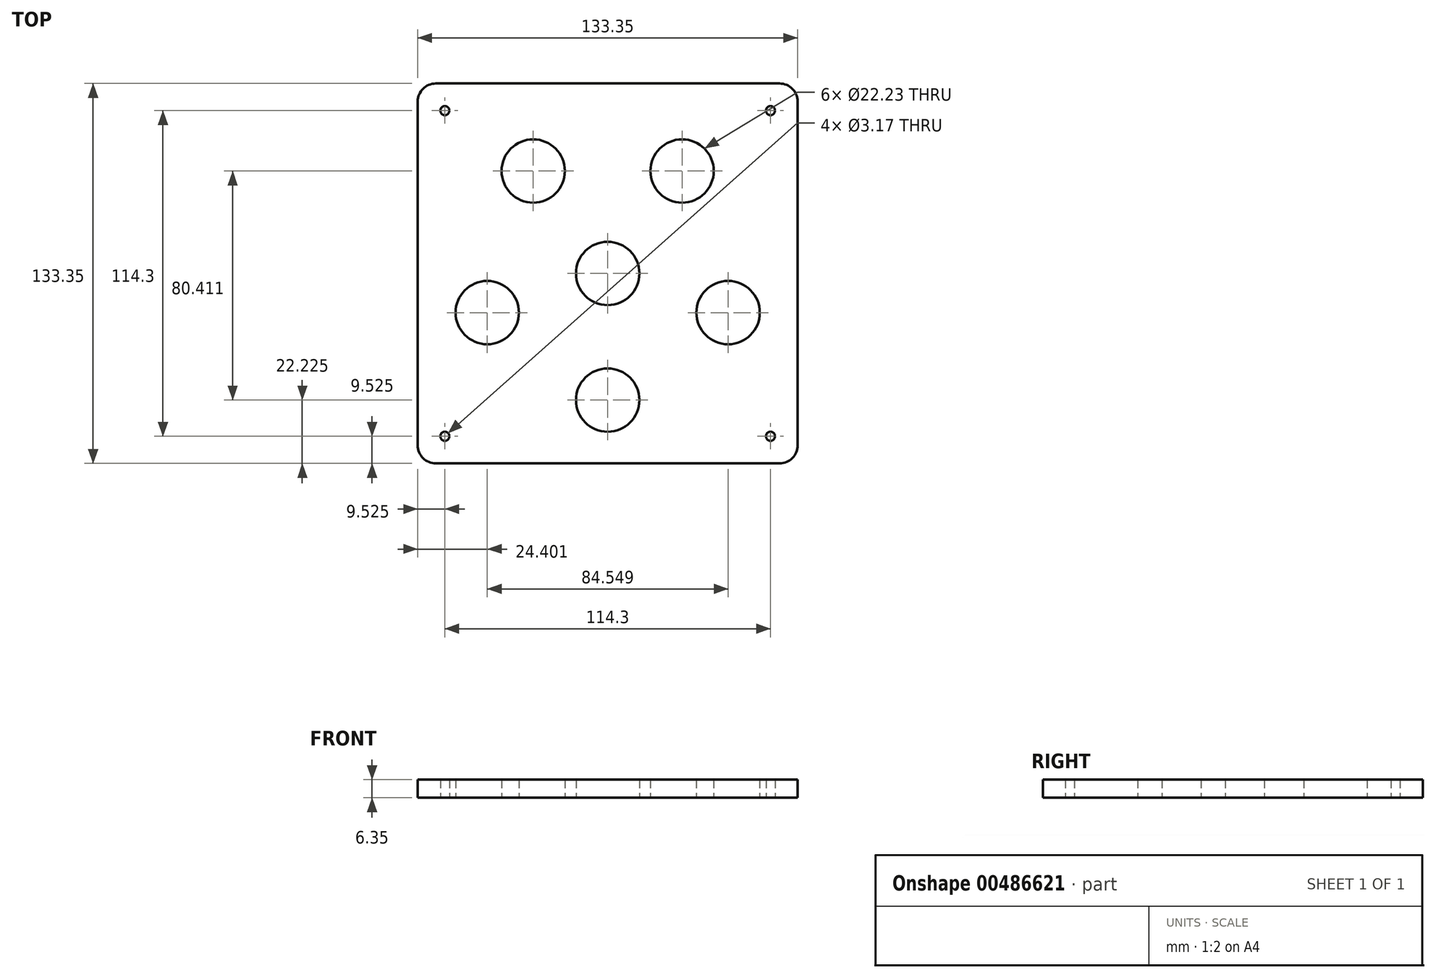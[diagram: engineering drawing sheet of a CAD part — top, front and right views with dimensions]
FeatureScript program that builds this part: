
annotation { "Feature Type Name" : "Feature", "Feature Type Description" : "" }
export const myFeature = defineFeature(function(context is Context, id is Id, definition is map)
    precondition{}
    {
        {
            var Q0;
            Q0=qCreatedBy(makeId("Top.planeOp"),FACE);
            var sketch = newSketch(context, id + "F0", { "sketchPlane" : qUnion([Q0])});
            skLineSegment(sketch, "E0.bottom", {"start": v(6.35, 0) * mm, "end": v(127, 0) * mm});
            skLineSegment(sketch, "E0.top", {"start": v(6.35, 133.35) * mm, "end": v(127, 133.35) * mm});
            skLineSegment(sketch, "E0.left", {"start": v(0, 6.35) * mm, "end": v(0, 127) * mm});
            skLineSegment(sketch, "E0.right", {"start": v(133.35, 6.35) * mm, "end": v(133.35, 127) * mm});
            skCircle(sketch, "E1", {"center": v(9.52, 123.83) * mm, "radius": 1.59 * mm});
            skCircle(sketch, "E2", {"center": v(123.83, 123.83) * mm, "radius": 1.59 * mm});
            skCircle(sketch, "E3", {"center": v(123.83, 9.53) * mm, "radius": 1.59 * mm});
            skCircle(sketch, "E4", {"center": v(9.52, 9.52) * mm, "radius": 1.59 * mm});
            skPoint(sketch, "E5", {"position": v(66.67, 66.68) * mm});
            skCircle(sketch, "E6", {"center": v(24.4, 52.94) * mm, "radius": 11.11 * mm});
            skCircle(sketch, "E7.1.0", {"center": v(66.68, 22.23) * mm, "radius": 11.11 * mm});
            skCircle(sketch, "E7.2.0", {"center": v(108.95, 52.94) * mm, "radius": 11.11 * mm});
            skCircle(sketch, "E7.3.0", {"center": v(92.8, 102.64) * mm, "radius": 11.11 * mm});
            skCircle(sketch, "E7.4.0", {"center": v(40.55, 102.64) * mm, "radius": 11.11 * mm});
            skPoint(sketch, "E8.visualSharp", {"position": v(0, 133.35) * mm});
            skArc(sketch, "E8.filletArc", {"start": v(6.35, 133.35) * mm, "mid": v(1.86, 131.5) * mm, "end": v(0, 127) * mm});
            skPoint(sketch, "E9.visualSharp", {"position": v(133.35, 133.35) * mm});
            skArc(sketch, "E9.filletArc", {"start": v(133.35, 127) * mm, "mid": v(131.5, 131.5) * mm, "end": v(127, 133.35) * mm});
            skPoint(sketch, "E10.visualSharp", {"position": v(0, 0) * mm});
            skArc(sketch, "E10.filletArc", {"start": v(0, 6.35) * mm, "mid": v(1.86, 1.86) * mm, "end": v(6.35, 0) * mm});
            skPoint(sketch, "E11.visualSharp", {"position": v(133.35, 0) * mm});
            skArc(sketch, "E11.filletArc", {"start": v(127, 0) * mm, "mid": v(131.5, 1.86) * mm, "end": v(133.35, 6.35) * mm});
            skCircle(sketch, "E12", {"center": v(66.67, 66.68) * mm, "radius": 11.11 * mm});
            skSolve(sketch);
        }
        {
            var Q0;
            Q0 = qSketchRegion(id + "F0", true);
            extrude(context, id + "F1", {"entities" : qUnion([Q0]), "depth" : 6.35 * mm});
        }
    });
